# Revit family: Hook-Bradley_Corp-Elvari-9B1-110000
name_source: partatom
category: Specialty Equipment
units: mm (PartAtom-declared; Revit-internal decimal feet)

## family parameters
Always vertical = No
Cut with Voids When Loaded = No
Maintain Annotation Orientation = No
Part Type = Normal
Room Calculation Point = No
Round Connector Dimension = Use Diameter
Shared = Yes
Work Plane-Based = No

## types (2) — shared parameters
Default Elevation = 0' - 0"
Description = ELVARI COAT / ROBE HOOK
Design Status = 1
Manufacturer = Bradley Corporation
Manufacturer Installation URL - English = https://www.bradleycorp.com
Model = 9B1-110000
Product Page URL = https://www.bradleycorp.com
Product Tech Data URL - English = https://www.bradleycorp.com
Specifications URL = https://www.bradleycorp.com
Version = 4

## type names (no varying parameters)
- 9B1-110000
- 9B1-110000_Simplify_1

## geometry (parser evidence)
native form markers: Blend x4, Sweep x2
no freeform markers — native parametric forms only
